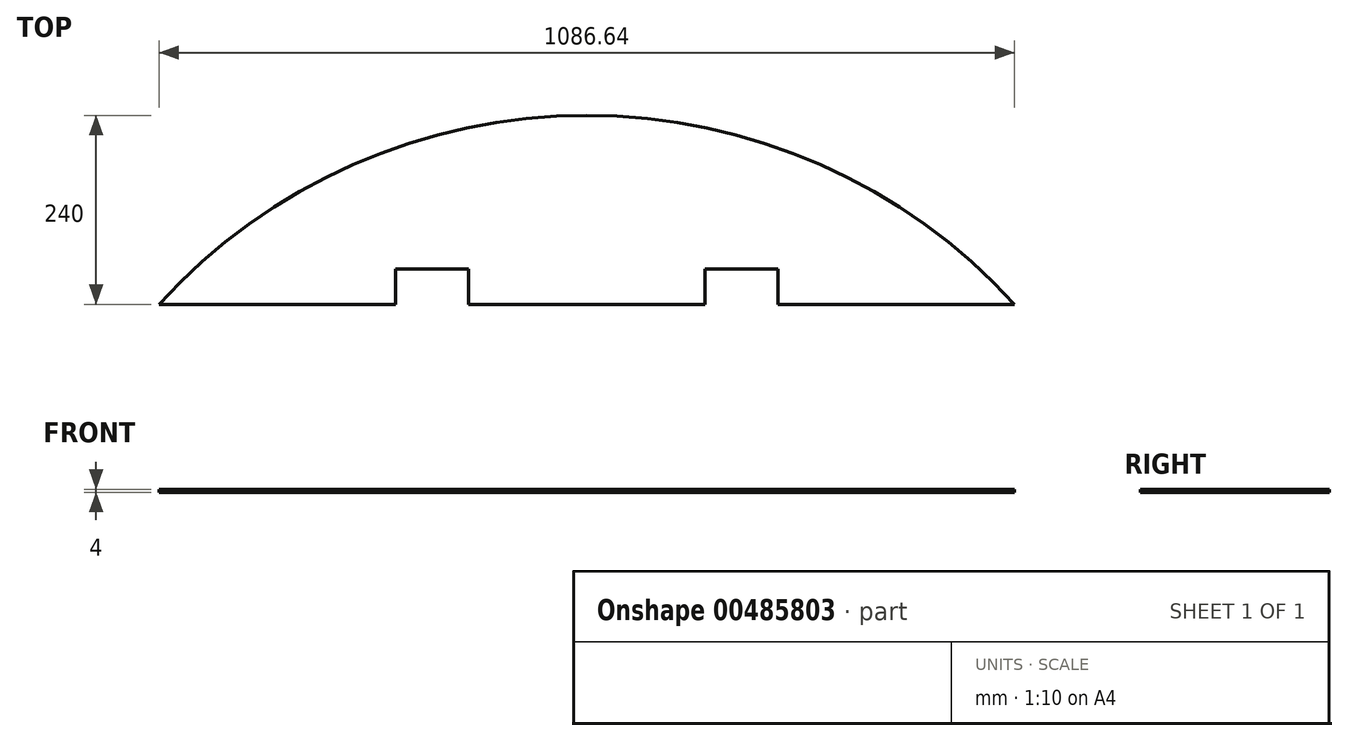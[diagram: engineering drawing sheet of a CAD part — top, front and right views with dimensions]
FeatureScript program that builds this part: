
annotation { "Feature Type Name" : "Feature", "Feature Type Description" : "" }
export const myFeature = defineFeature(function(context is Context, id is Id, definition is map)
    precondition{}
    {
        {
            var Q0;
            Q0=qCreatedBy(makeId("Top.planeOp"),FACE);
            var sketch = newSketch(context, id + "F0", { "sketchPlane" : qUnion([Q0])});
            skArc(sketch, "E0", {"start": v(543.32, 495) * mm, "mid": v(0, 735) * mm, "end": v(-543.32, 495) * mm});
            skLineSegment(sketch, "E1", {"start": v(-543.32, 495) * mm, "end": v(543.32, 495) * mm});
            skSolve(sketch);
        }
        {
            var Q0;
            Q0 = qSketchRegion(id + "F0", true);
            extrude(context, id + "F1", {"entities" : qUnion([Q0]), "depth" : 4 * mm});
        }
        {
            var Q0;
            Q0=makeQuery(id+"F1.opExtrude","CAP_FACE",FACE,{"disambiguationData":[OSD([sQuery(id+"F0.wireOp",EDGE,"E0"),sQuery(id+"F0.wireOp",EDGE,"E1")])],"isStart":false});
            var sketch = newSketch(context, id + "F2", { "sketchPlane" : qUnion([Q0])});
            skLineSegment(sketch, "E2.bottom", {"start": v(150, 495) * mm, "end": v(243, 495) * mm});
            skLineSegment(sketch, "E2.top", {"start": v(150, 540) * mm, "end": v(243, 540) * mm});
            skLineSegment(sketch, "E2.left", {"start": v(150, 495) * mm, "end": v(150, 540) * mm});
            skLineSegment(sketch, "E2.right", {"start": v(243, 495) * mm, "end": v(243, 540) * mm});
            skLineSegment(sketch, "E3", {"start": v(0, 452.13) * mm, "end": v(0, 733.44) * mm, "construction": true});
            skPoint(sketch, "E3.endSnap0", {"position": v(0, 735) * mm});
            skLineSegment(sketch, "E4.MirrorCS", {"start": v(-243, 495) * mm, "end": v(-243, 540) * mm});
            skLineSegment(sketch, "E5.MirrorCS", {"start": v(-150, 495) * mm, "end": v(-150, 540) * mm});
            skLineSegment(sketch, "E6.MirrorCS", {"start": v(-150, 540) * mm, "end": v(-243, 540) * mm});
            skLineSegment(sketch, "E7.MirrorCS", {"start": v(-150, 495) * mm, "end": v(-243, 495) * mm});
            skSolve(sketch);
        }
        {
            var Q0;
            Q0 = qSketchRegion(id + "F2", true);
            extrude(context, id + "F3", {"entities" : qUnion([Q0]), "operationType" : NewBodyOperationType.REMOVE, "oppositeDirection" : true, "depth" : 25 * mm});
        }
    });
